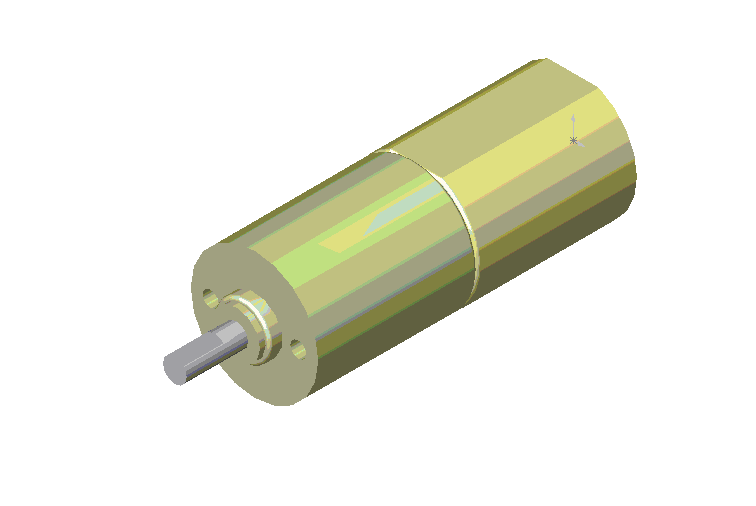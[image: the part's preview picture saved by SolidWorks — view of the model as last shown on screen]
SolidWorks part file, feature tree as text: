
SOLIDWORKS PART (.sldprt)
format: sldprt  version: not decoded by parser v0  size: 390,656 bytes
history: native  units: mm
features: sketch x9, extrude x6, fillet x2, cut_extrude x1, hole x1, pattern_circular x1 (+8 scaffold rows collapsed)
feature tree (28):
  scaffold x8  (default folders/planes/origin — collapsed)
  sketch  "Sketch1"  dims[D1=8.0mm D2=7.325mm D3=7.325mm]
  extrude  "Motor Body"  Depth=20mm
  fillet  "Fillet2"  Radius=0.4mm
  sketch  "Sketch10"  dims[D1=3.5mm]
  extrude  "Motor Back"  Depth=1mm
  sketch  "Sketch3"
  extrude  "Gear Box"  Depth=20mm
  sketch  "Sketch4"  dims[D1=7.0mm]
  extrude  "Front Nub"  Depth=1.6mm
  sketch  "Sketch5"  dims[D1=~3.039087mm]
  extrude  "Front Nub2"  Depth=0.7mm
  sketch  "Sketch6"  dims[D1=~1.071585mm]
  extrude  "Shaft"  Depth=7.7mm
  sketch  "Sketch7"  dims[D1=1.0mm]
  cut_extrude  "Shaft Flat"  Depth=5mm
  hole  "Mount Hole"  Diameter=1.6mm Depth=2.999994mm
  sketch  "Sketch9"  dims[D1=5.5mm]
  sketch  "Sketch8"  dims[hole-wizard template sketch: 28 standard entries collapsed; hole parameters kept: c8.Tap Drill Dia.=1.6mm c8.Tap Drill Depth=~2.999994mm c8.Thread Dia.=2.0mm c8.Thread Depth=~3.999992mm c8.D5=~14.816244mm c8.Drill Angle=118.0deg]
  pattern_circular  "CirPattern1"  Count=2 Angle=360deg
  fillet  "Fillet3"  Radius=0.4mm
decode coverage: 19 of 20 modeling features carry decoded parameters
note: ~ marks probable driven/reference dimensions
note: suppression state not decoded; provenance and decode notes live in map.json
